# Revit family: Hand-Shower-Set_Contemporary_Kiwami-Renesse_TS170F_TOTO
name_source: partatom
category: Plumbing Fixtures
revit_build: Autodesk Revit Architecture 2013 (Build: 20130531_2115(x64)
units: mm (PartAtom-declared; Revit-internal decimal feet)

## types (1)
- TS170F
    04 CSI = 22 41 39
    95 CSI = 15416
    Assembly Code = D2010710
    CAD Drawing URL = http://assets.totousa.com
    CW Connection = Yes
    CWFU = 0
    Color Availability = #CP Polished Chrome
    Default Elevation = 3' - 10 7/8"
    Depth = 0' - 2 17/32"
    Description = Handshower Trim Set
    Finish = Metal - TOTO - Chrome - Polished
    Flow Rate = 0 GPM
    HW Connection = Yes
    HWFU = 0
    Height = 2' - 10 3/32"
    Horizontal Distance from Control to Handshower = 0' - 2"
    Hot Water Connection = Hot Water Connection
    Manufacturer = TOTO USA, Inc.
    Manufacturer Fax = (770) 282-0002
    Model = TS170F
    Series = Kiwami Renesse
    Shipping Weight = 8.30 lb
    Spec Sheet URL = http://assets.totousa.com
    Style = Contemporary
    Subcategory = Showers
    Tempered Water Connection Diameter = 0' - 1"
    Tempered Water Connection NPT = 1"
    Toto BIM Number = BM-00213
    URL = http://www.totousa.com
    Vent Connection = No
    Vertical Distance from Control to Handshower = 2' - 0"
    WFU = 0
    Warranty = Lifetime Limited Warranty (Residential Use); One Year Limited (Commercial Use)
    Warranty URL = http://www.totousa.com
    Waste Connection = No
    Width = 0' - 6 17/32"

## geometry (parser evidence)
native form markers: Blend x2, Sweep x4
no freeform markers — native parametric forms only
